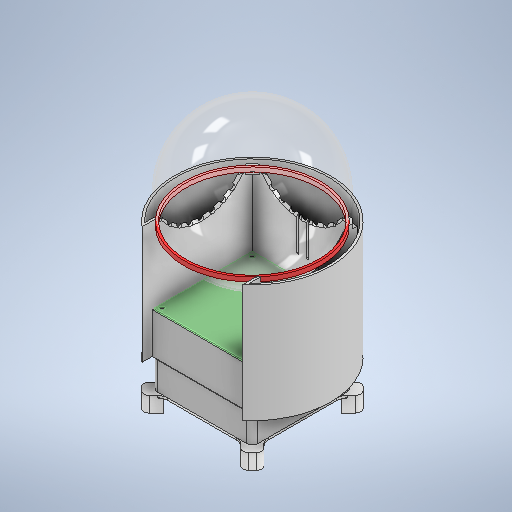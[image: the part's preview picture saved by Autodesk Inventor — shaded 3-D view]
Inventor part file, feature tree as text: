
AUTODESK INVENTOR PART (.ipt)
format: ipt  version: 2025.2 (Build 292293000, 293)  size: 1,617,408 bytes
history: native  units: in
note: dims shown in document units (in); Inventor stores cm internally (conversion verified against a paired STEP export)
features: extrude x21, sketch x17, projected_geometry x15, other x5, fillet x3, plane x2, revolve x2, pattern_circular x2, mirror x1, helix x1
ambient origin geometry x8: Origin, YZ Plane, XZ Plane, XY Plane, X Axis, Y Axis, Z Axis, Center Point
bodies: Body1 (feature_tree), Body2 (feature_tree), Body3 (feature_tree), Body4 (feature_tree), Body5 (feature_tree), Body6 (feature_tree)
feature tree (69):
  other  "Fan"
  extrude  "Extrusion1"  Depth=3.622in
  fillet  "Fillet1"  Radius=0.1772in
  plane  "Work Plane1"
  extrude  "Extrusion2"  Depth=0.1772in
  plane  "Work Plane2"
  extrude  "Extrusion3"  Depth=3.5039in
  sketch  "Sketch5"  dims[d11=1.4567in d12=3.5433in]
  revolve  "Revolution1"  [1 undecoded]
  extrude  "Extrusion4"  Depth=3.5433in
  sketch  "Sketch7"  dims[d16=4.7803in d17=0.0787in]
  extrude  "Extrusion5"  Depth=2.5591in
  extrude  "Extrusion6"  Depth=0.0787in
  sketch  "Sketch8"  dims[d18=0.1575in d19=0.0in d20=5.1181in]
  extrude  "Extrusion7"  Depth=0.1575in
  extrude  "Extrusion8"  TaperAngle=90.0deg  [1 undecoded]
  extrude  "Extrusion10"  Depth=0.0787in
  sketch  "Sketch11"  dims[d23=0.0394in d24=0.0787in]
  extrude  "Extrusion11"  Depth=0.0787in
  sketch  "Sketch12"  dims[d25=0.1575in d26=0.0in d27=0.0787in]
  extrude  "Extrusion12"  Depth=0.0787in TaperAngle=0.0deg
  extrude  "Extrusion13"  Depth=0.0787in
  extrude  "Extrusion15"  Depth=0.3937in TaperAngle=0.0deg
  extrude  "Extrusion16"  Depth=0.0787in
  pattern_circular  "Circular Pattern1"  [2 undecoded]
  extrude  "Extrusion17"  Depth=0.0787in
  revolve  "Revolution2"  [1 undecoded]
  extrude  "Extrusion18"  Depth=0.0787in
  extrude  "Extrusion19"  Depth=0.3937in TaperAngle=0.0deg
  extrude  "Extrusion20"  Depth=0.1181in TaperAngle=0.0deg
  pattern_circular  "Circular Pattern2"  [2 undecoded]
  extrude  "Extrusion21"  Depth=0.3937in
  sketch  "Sketch19"  dims[d45=0.1496in d46=0.0787in d47=0.0787in d48=0.0787in d49=0.0787in d50=0.3937in d51=0.0in d52=0.1181in d53=0.0in d56=0.3937in d57=0.0in d58=0.7874in d59=0.7874in d60=0.7874in d61=0.9843in d62=0.9843in d63=0.1181in d64=0.0in d65=1.1811in d66=-1.2368in d68=0.1181in d69=0.0in d70=90.0deg d71=0.3937in d72=0.0in d73=0.3937in d74=0.0in d75=0.2756in d76=0.4331in d77=0.7087in d78=2.5591in d81=0.1969in d82=2.7559in d84=0.5497in d86=0.1969in d87=0.0in d88=1.1811in d89=180.0deg d91=0.3937in d92=0.0in d93=0.5906in d94=0.0787in d95=0.0in d96=0.5512in d97=0.0in d98=0.1969in d99=0.3937in]
  extrude  "Extrusion22"  Depth=0.3937in
  extrude  "Extrusion23"  Depth=0.3937in
  mirror  "Mirror1"
  fillet  "Fillet2"  Radius=0.9843in
  fillet  "Fillet3"  Radius=0.1181in
  sketch  "Sketch1"  dims[d1=3.622in d2=3.248in d3=0.1772in]
  sketch  "Sketch2"  dims[d6=0.1772in d7=3.5039in]
  other  "PCB"
  sketch  "Sketch4"  dims[d8=1.0in d9=0.0in d10=0.1969in]
  helix  "Coil"  [1 undecoded]
  projected_geometry  "Projected Loop1"
  other  "Globe"
  sketch  "Sketch6"  dims[d13=0.063in d14=0.0in d15=2.5591in]
  projected_geometry  "Projected Loop2"
  other  "Shroud"
  projected_geometry  "Projected Loop3"
  projected_geometry  "Projected Loop4"
  projected_geometry  "Projected Loop5"
  projected_geometry  "Projected Loop6"
  sketch  "Sketch9"  dims[d21=0.0591in d22=90.0deg]
  projected_geometry  "Projected Loop7"
  projected_geometry  "Projected Loop9"
  projected_geometry  "Projected Loop10"
  sketch  "Sketch13"  dims[d28=0.0787in d29=0.0in d30=0.0787in d31=0.0in]
  projected_geometry  "Projected Loop11"
  sketch  "Sketch14"  dims[d32=0.1969in d33=0.0787in]
  projected_geometry  "Projected Loop12"
  projected_geometry  "Projected Loop13"
  projected_geometry  "Projected Loop14"
  sketch  "Sketch15"  dims[d34=0.3937in d35=0.0in d36=0.3937in d37=0.0in]
  projected_geometry  "Projected Loop15"
  sketch  "Sketch17"  dims[d40=0.3937in d41=0.0in d42=0.0787in]
  sketch  "Sketch18"  dims[d43=0.3937in d44=0.0in]
  sketch  "Sketch Circular Pattern1"  dims[d4=0.1772in d5=0.1772in]
  projected_geometry  "Projected Loop16"
  other  "Foot"
note: 8 required parameter values undecoded (feature->parameter linkage not recoverable at this tier; creation-order binding heuristic only, values carry confidence <= 0.55)